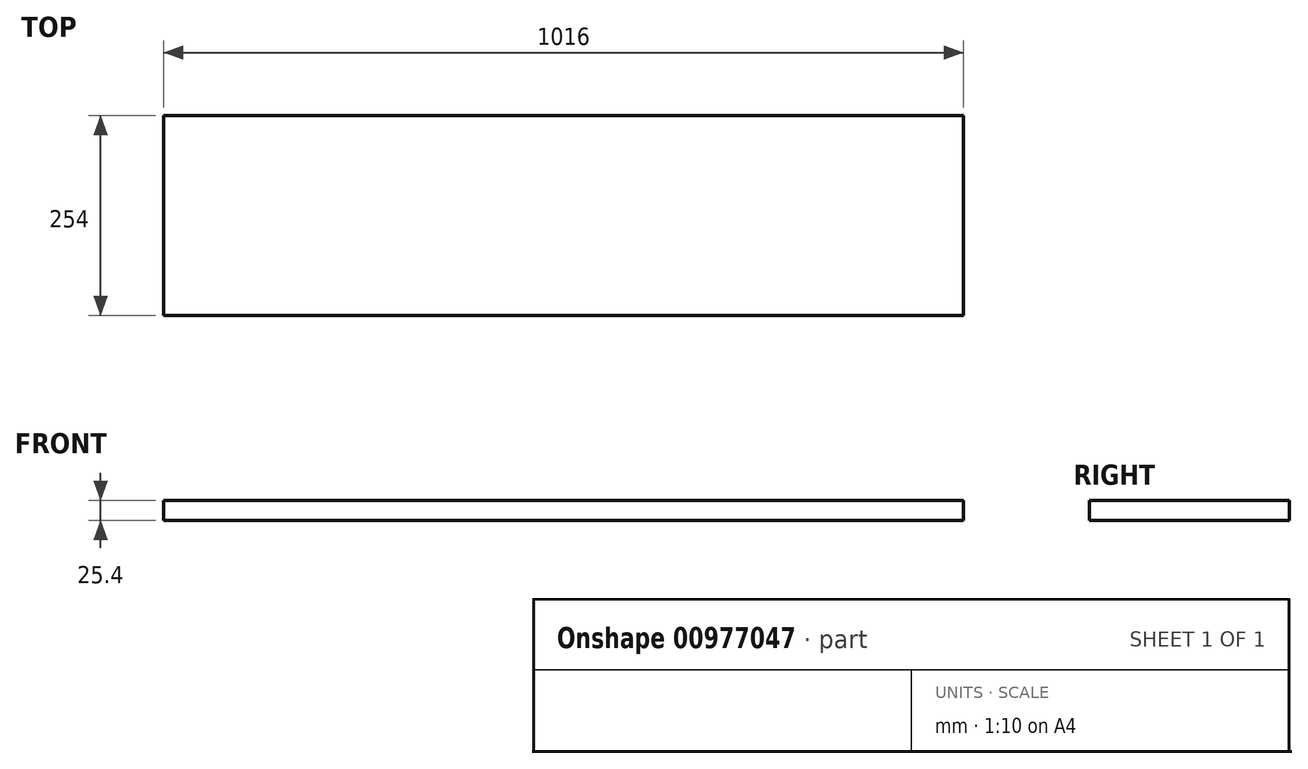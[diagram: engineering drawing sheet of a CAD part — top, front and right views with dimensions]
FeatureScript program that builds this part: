
annotation { "Feature Type Name" : "Feature", "Feature Type Description" : "" }
export const myFeature = defineFeature(function(context is Context, id is Id, definition is map)
    precondition{}
    {
        {
            var Q0;
            Q0=qCreatedBy(makeId("Top.planeOp"),FACE);
            var sketch = newSketch(context, id + "F0", { "sketchPlane" : qUnion([Q0])});
            skLineSegment(sketch, "E0.bottom", {"start": v(0, 0) * mm, "end": v(-1016, 0) * mm});
            skLineSegment(sketch, "E0.top", {"start": v(0, 254) * mm, "end": v(-1016, 254) * mm});
            skLineSegment(sketch, "E0.left", {"start": v(0, 0) * mm, "end": v(0, 254) * mm});
            skLineSegment(sketch, "E0.right", {"start": v(-1016, 0) * mm, "end": v(-1016, 254) * mm});
            skSolve(sketch);
        }
        {
            var Q0;
            Q0=makeQuery(id+"F0.imprint","IMPRINT",FACE,{"disambiguationData":[TD([[makeQuery(id+"F0.imprint","IMPRINT",EDGE,{"derivedFrom":sQuery(id+"F0.wireOp",EDGE,"E0.bottom")}),-1.0]])]});
            extrude(context, id + "F1", {"entities" : qUnion([Q0]), "depth" : 25.4 * mm, "offsetDistance" : 25.4 * mm});
        }
    });
